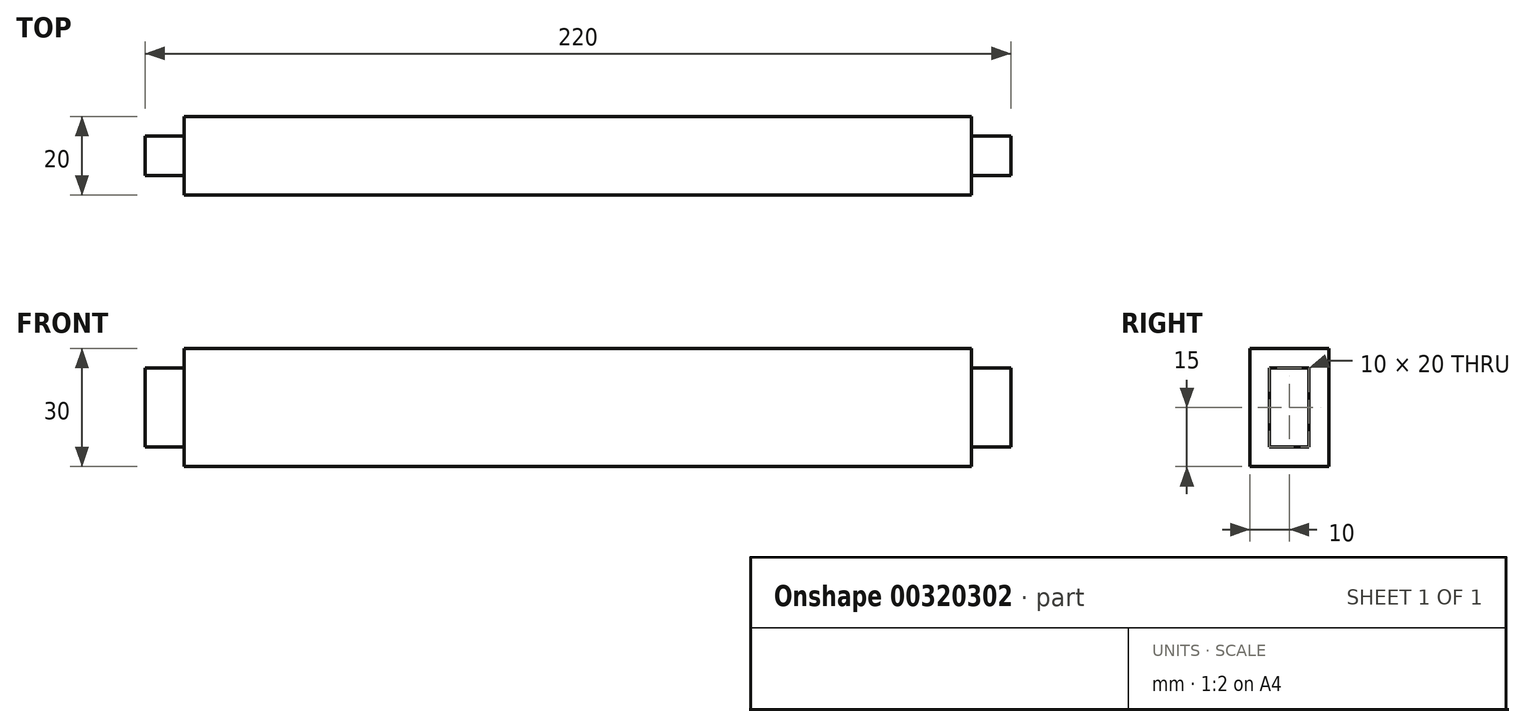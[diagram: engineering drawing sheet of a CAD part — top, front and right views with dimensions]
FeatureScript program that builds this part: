
annotation { "Feature Type Name" : "Feature", "Feature Type Description" : "" }
export const myFeature = defineFeature(function(context is Context, id is Id, definition is map)
    precondition{}
    {
        {
            var Q0;
            Q0=qCreatedBy(makeId("Front.planeOp"),FACE);
            var sketch = newSketch(context, id + "F0", { "sketchPlane" : qUnion([Q0])});
            skLineSegment(sketch, "E0.bottom", {"start": v(-100, 15) * mm, "end": v(100, 15) * mm});
            skLineSegment(sketch, "E0.top", {"start": v(-100, -15) * mm, "end": v(100, -15) * mm});
            skLineSegment(sketch, "E0.left", {"start": v(-100, 15) * mm, "end": v(-100, -15) * mm});
            skLineSegment(sketch, "E0.right", {"start": v(100, 15) * mm, "end": v(100, -15) * mm});
            skPoint(sketch, "E0.middle", {"position": v(0, 0) * mm});
            skSolve(sketch);
        }
        {
            var Q0;
            Q0=makeQuery(id+"F0.imprint","IMPRINT",FACE,{"disambiguationData":[TD([[makeQuery(id+"F0.imprint","IMPRINT",EDGE,{"derivedFrom":sQuery(id+"F0.wireOp",EDGE,"E0.bottom")}),-1.0]])]});
            extrude(context, id + "F1", {"entities" : qUnion([Q0]), "depth" : 20 * mm});
        }
        {
            var Q0;
            Q0=makeQuery(id+"F1.opExtrude","SWEPT_FACE",FACE,{"disambiguationData":[OSD([sQuery(id+"F0.wireOp",EDGE,"E0.left")])]});
            var sketch = newSketch(context, id + "F2", { "sketchPlane" : qUnion([Q0])});
            skLineSegment(sketch, "E1.bottom", {"start": v(5, 10) * mm, "end": v(15, 10) * mm});
            skLineSegment(sketch, "E1.top", {"start": v(5, -10) * mm, "end": v(15, -10) * mm});
            skLineSegment(sketch, "E1.left", {"start": v(5, 10) * mm, "end": v(5, -10) * mm});
            skLineSegment(sketch, "E1.right", {"start": v(15, 10) * mm, "end": v(15, -10) * mm});
            skPoint(sketch, "E1.middle", {"position": v(10, 0) * mm});
            skLineSegment(sketch, "E2", {"start": v(0, 0) * mm, "end": v(5, 0) * mm, "construction": true});
            skLineSegment(sketch, "E3", {"start": v(10, 15) * mm, "end": v(10, 10) * mm, "construction": true});
            skLineSegment(sketch, "E4", {"start": v(10, -15) * mm, "end": v(10, -10) * mm, "construction": true});
            skLineSegment(sketch, "E5", {"start": v(20, 0) * mm, "end": v(15, 0) * mm, "construction": true});
            skSolve(sketch);
        }
        {
            var Q0;
            Q0=makeQuery(id+"F2.imprint","IMPRINT",FACE,{"disambiguationData":[TD([[makeQuery(id+"F2.imprint","IMPRINT",EDGE,{"derivedFrom":sQuery(id+"F2.wireOp",EDGE,"E1.bottom")}),-1.0]])]});
            extrude(context, id + "F3", {"entities" : qUnion([Q0]), "operationType" : NewBodyOperationType.ADD, "depth" : 10 * mm});
        }
        {
            var Q0;
            Q0=makeQuery(id+"F1.opExtrude","SWEPT_BODY",BODY,{"disambiguationData":[OSD([sQuery(id+"F0.wireOp",EDGE,"E0.bottom"),sQuery(id+"F0.wireOp",EDGE,"E0.top"),sQuery(id+"F0.wireOp",EDGE,"E0.left"),sQuery(id+"F0.wireOp",EDGE,"E0.right")])]});
            var Q1;
            Q1=qCreatedBy(makeId("Right.planeOp"),FACE);
            mirror(context, id + "F4", {"operationType" : NewBodyOperationType.ADD, "entities" : qUnion([Q0]), "mirrorPlane" : qUnion([Q1])});
        }
    });
